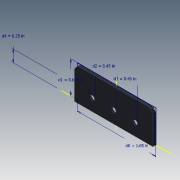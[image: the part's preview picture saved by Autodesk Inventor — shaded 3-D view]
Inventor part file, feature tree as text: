
AUTODESK INVENTOR PART (.ipt)
format: ipt  version: 2020.3 (Build 243373000, 373)  size: 110,080 bytes
history: native  units: in
note: dims shown in document units (in); Inventor stores cm internally (conversion verified against a paired STEP export)
features: sketch x1, extrude x1, fillet x1, hole x1
ambient origin geometry x8: Origin, YZ Plane, XZ Plane, XY Plane, X Axis, Y Axis, Z Axis, Center Point
bodies: Solid1 (feature_tree)
feature tree (4):
  sketch  "Sketch1"  dims[d0=1.65in d1=0.675in d2=0.45in d3=0.45in d4=0.25in d5=0.06in d6=0.0in d7=0.125in d8=0.096in d9=0.75in d10=0.172in d11=0.25in d12=0.5635in d13=1.0in d14=0.8108in]
  extrude  "Extrusion1"  Depth=0.675in
  fillet  "Fillet1"  Radius=0.45in
  hole  "Hole1"  [1 undecoded]
note: 1 required parameter value undecoded (feature->parameter linkage not recoverable at this tier; creation-order binding heuristic only, values carry confidence <= 0.55)
